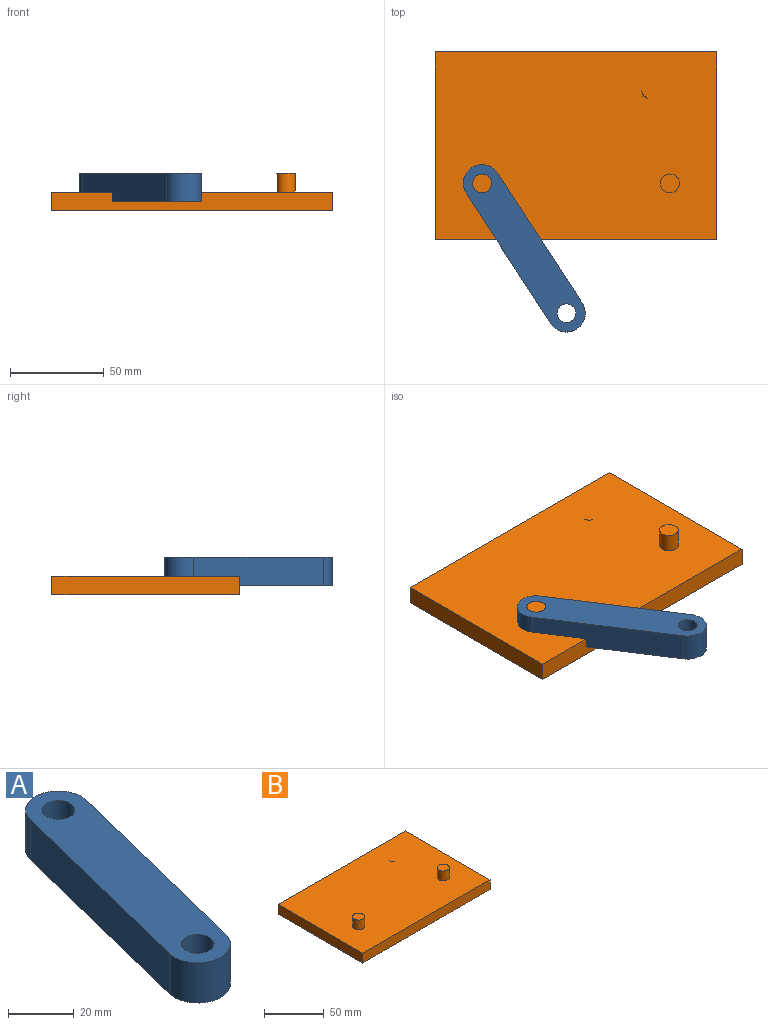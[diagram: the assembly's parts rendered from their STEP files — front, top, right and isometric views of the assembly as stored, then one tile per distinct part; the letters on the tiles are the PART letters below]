
ASSEMBLY  parts=2 mates=1
PART A: 8 faces, bbox 40x100x15 mm
  f0: cylinder r=10mm len=19.7mm, axis (0,0,-1), area 471.2mm2, adj f1,f2,f4,f5
  f1: plane 80x20mm, normal (-0.97,0.24,0), area 1236.9mm2, adj f0,f3,f4,f5
  f2: plane 80x20mm, normal (0.97,-0.24,0), area 1236.9mm2, adj f0,f3,f4,f5
  f3: cylinder r=10mm len=19.7mm, axis (0,0,-1), area 471.2mm2, adj f1,f2,f4,f5
  f4: plane 100x40mm, normal (0,0,1), area 1806.3mm2, adj f0,f1,f2,f3,f6,f7
  f5: plane 100x40mm, normal (0,0,-1), area 1806.3mm2, adj f0,f1,f2,f3,f6,f7
  f6: cylinder r=5mm len=15mm, axis (0,0,-1), area 471.2mm2, adj f4,f5
  f7: cylinder r=5mm len=15mm, axis (0,0,-1), area 471.2mm2, adj f4,f5
PART B: 13 faces, bbox 150x100x20 mm
  f0: plane 10x2.42mm, normal (0.39,0.92,0), area 26.3mm2, adj f1,f6,f7,f8
  f1: plane 10x2.58mm, normal (0.98,0.2,0), area 26.3mm2, adj f0,f6,f7,f8
  f2: plane 150x10mm, normal (0,1,0), area 1500mm2, adj f3,f5,f7,f8
  f3: plane 100x10mm, normal (-1,0,0), area 1000mm2, adj f2,f4,f7,f8
  f4: plane 150x10mm, normal (0,-1,0), area 1500mm2, adj f3,f5,f7,f8
  f5: plane 100x10mm, normal (1,0,0), area 1000mm2, adj f2,f4,f7,f8
  f6: cylinder r=5mm len=10mm, axis (0,0,1), area 48.4mm2, adj f0,f1,f7,f8
  f7: plane 150x100mm, normal (0,0,-1), area 14999mm2, adj f0,f1,f2,f3,f4,f5,f6
  f8: plane 150x100mm, normal (0,0,1), area 14841.9mm2, adj f0,f1,f2,f3,f4,f5,f6,f9
  f9: cylinder r=5mm len=10mm, axis (0,0,-1), area 314.2mm2, adj f8,f10
  f10: plane 10x10mm, normal (0,0,1), area 78.5mm2, adj f9
  f11: cylinder r=5mm len=10mm, axis (0,0,-1), area 314.2mm2, adj f8,f12
  f12: plane 10x10mm, normal (0,0,1), area 78.5mm2, adj f11
PLACE A rot(axis=(0,0,-1),133deg) t=(-53.97,-89.76,9.45)mm
PLACE B t=(15.46,-19.54,14.45)mm
MATE revolute A.f3 <-> B.f9  axis (0,0,1) through (-34.54,-39.54,24.45)mm
